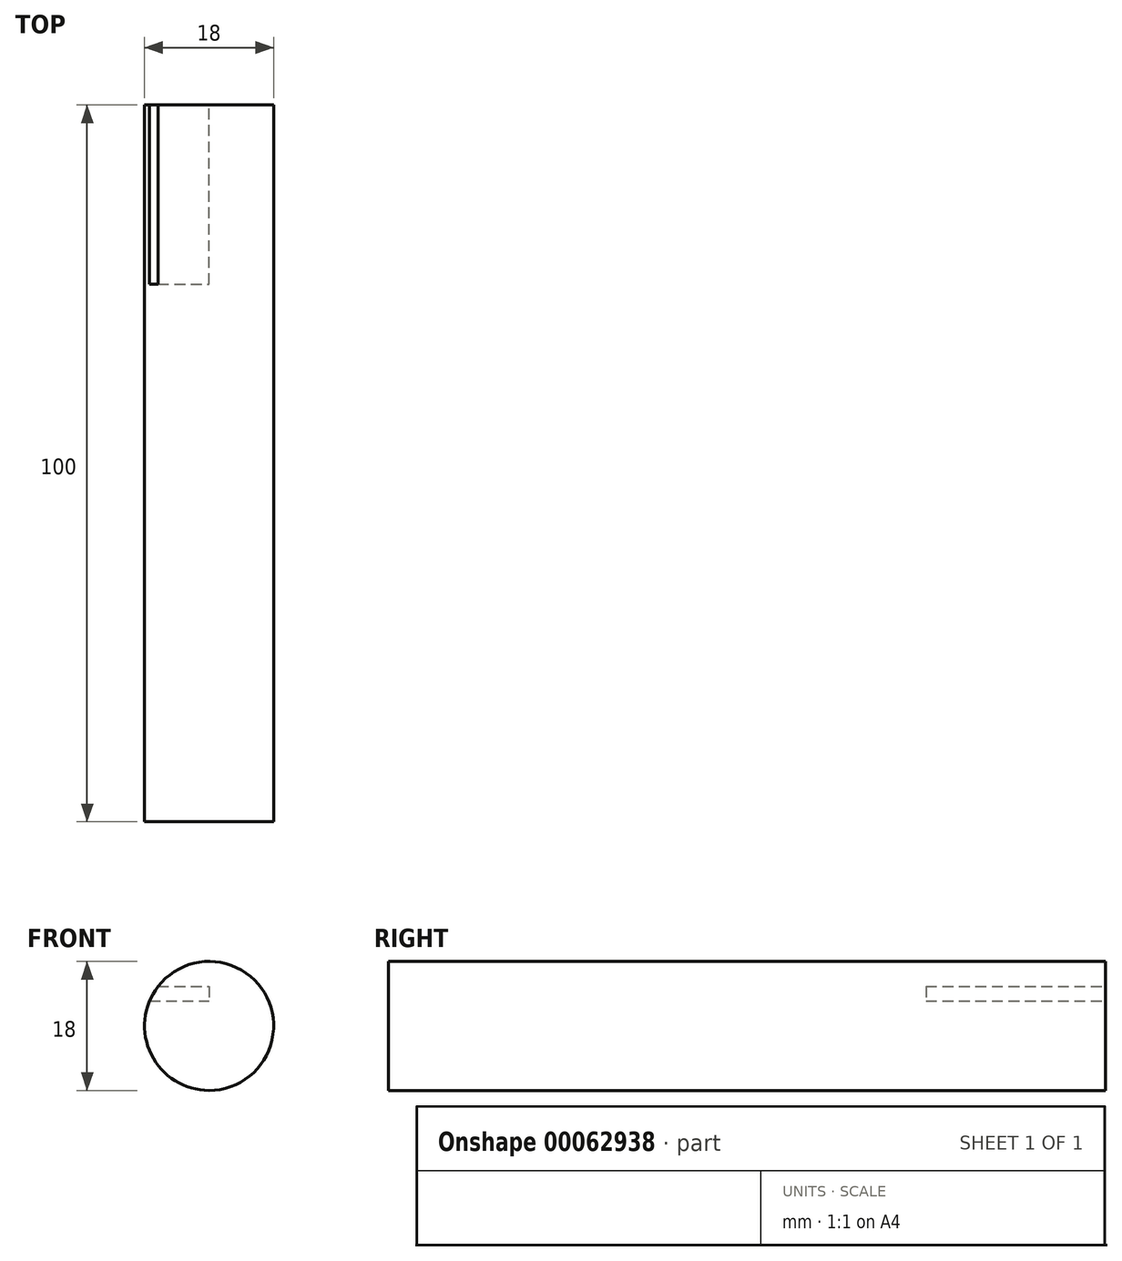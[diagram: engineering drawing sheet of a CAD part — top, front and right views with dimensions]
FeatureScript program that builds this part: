
annotation { "Feature Type Name" : "Feature", "Feature Type Description" : "" }
export const myFeature = defineFeature(function(context is Context, id is Id, definition is map)
    precondition{}
    {
        {
            var Q0;
            Q0=qCreatedBy(makeId("Front.planeOp"),FACE);
            var sketch = newSketch(context, id + "F0", { "sketchPlane" : qUnion([Q0])});
            skCircle(sketch, "E0", {"center": v(0, 0) * mm, "radius": 9 * mm});
            skSolve(sketch);
        }
        {
            var Q0;
            Q0 = qSketchRegion(id + "F0", true);
            extrude(context, id + "F1", {"entities" : qUnion([Q0]), "depth" : 100 * mm});
        }
        {
            var Q0;
            Q0=qCreatedBy(makeId("Front.planeOp"),FACE);
            var sketch = newSketch(context, id + "F2", { "sketchPlane" : qUnion([Q0])});
            skLineSegment(sketch, "E1", {"start": v(-10.73, 3.5) * mm, "end": v(0, 3.5) * mm});
            skLineSegment(sketch, "E2", {"start": v(-10.73, 3.5) * mm, "end": v(-10.73, 5.5) * mm});
            skLineSegment(sketch, "E3", {"start": v(-10.73, 5.5) * mm, "end": v(0, 5.5) * mm});
            skLineSegment(sketch, "E4", {"start": v(0, 5.5) * mm, "end": v(0, 3.5) * mm});
            skSolve(sketch);
        }
        {
            var Q0;
            Q0 = qSketchRegion(id + "F2", true);
            extrude(context, id + "F3", {"entities" : qUnion([Q0]), "operationType" : NewBodyOperationType.REMOVE, "depth" : 25 * mm});
        }
    });
